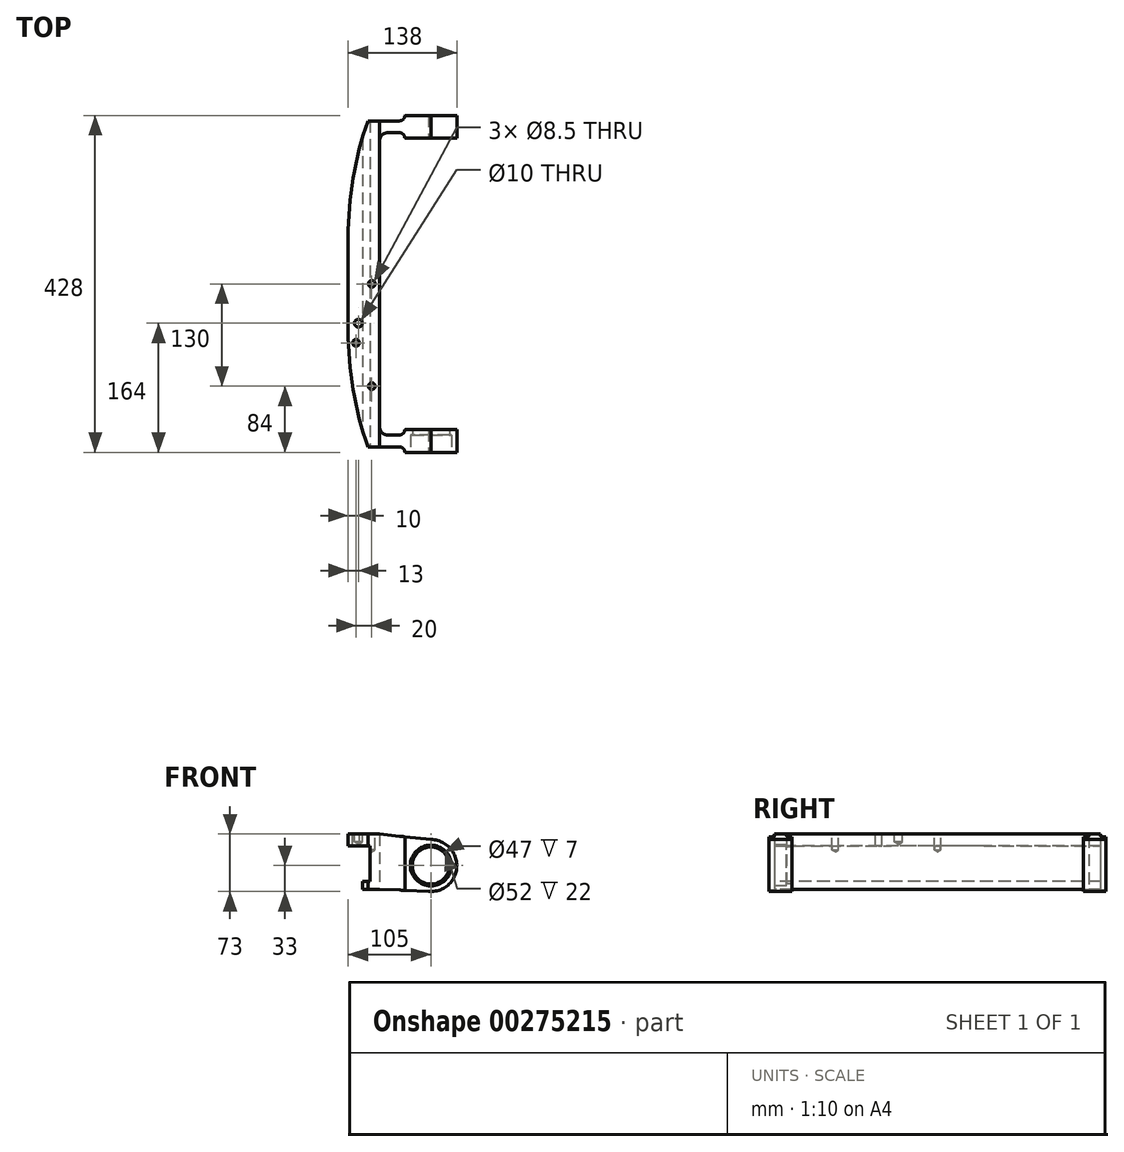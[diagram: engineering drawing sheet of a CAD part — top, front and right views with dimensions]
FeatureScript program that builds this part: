
annotation { "Feature Type Name" : "Feature", "Feature Type Description" : "" }
export const myFeature = defineFeature(function(context is Context, id is Id, definition is map)
    precondition{}
    {
        {
            var Q0;
            Q0=qCreatedBy(makeId("Top.planeOp"),FACE);
            var sketch = newSketch(context, id + "F0", { "sketchPlane" : qUnion([Q0])});
            skLineSegment(sketch, "E0", {"start": v(-134.94, 0) * mm, "end": v(159.57, 0) * mm, "construction": true});
            skLineSegment(sketch, "E1", {"start": v(0, 0) * mm, "end": v(0, 182) * mm});
            skLineSegment(sketch, "E2", {"start": v(-40, 0) * mm, "end": v(-40, 59) * mm});
            skLineSegment(sketch, "E3", {"start": v(10, 192) * mm, "end": v(25, 192) * mm});
            skLineSegment(sketch, "E4", {"start": v(32, 185) * mm, "end": v(32, 185) * mm});
            skLineSegment(sketch, "E5", {"start": v(32, 185) * mm, "end": v(98, 185) * mm});
            skLineSegment(sketch, "E6", {"start": v(98, 185) * mm, "end": v(98, 214) * mm});
            skLineSegment(sketch, "E7", {"start": v(98, 214) * mm, "end": v(32, 214) * mm});
            skLineSegment(sketch, "E8", {"start": v(32, 214) * mm, "end": v(32, 214) * mm});
            skLineSegment(sketch, "E9", {"start": v(25, 207) * mm, "end": v(-14.97, 207) * mm});
            skLineSegment(sketch, "E10", {"start": v(5.7, 199.5) * mm, "end": v(104.97, 199.5) * mm, "construction": true});
            skLineSegment(sketch, "E11.MirrorCS", {"start": v(-40, 0) * mm, "end": v(-40, -59) * mm});
            skLineSegment(sketch, "E12.MirrorCS", {"start": v(0, 0) * mm, "end": v(0, -182) * mm});
            skLineSegment(sketch, "E13.MirrorCS", {"start": v(10, -192) * mm, "end": v(32, -192) * mm});
            skLineSegment(sketch, "E14.MirrorCS", {"start": v(32, -207) * mm, "end": v(-14.97, -207) * mm});
            skLineSegment(sketch, "E15.MirrorCS", {"start": v(98, -214) * mm, "end": v(32, -214) * mm});
            skLineSegment(sketch, "E16.MirrorCS", {"start": v(32, -185) * mm, "end": v(98, -185) * mm});
            skLineSegment(sketch, "E17.MirrorCS", {"start": v(98, -185) * mm, "end": v(98, -214) * mm});
            skArc(sketch, "E18", {"start": v(-40, 59) * mm, "mid": v(-33.7, 134.05) * mm, "end": v(-14.97, 207) * mm});
            skArc(sketch, "E19.MirrorCS", {"start": v(-40, -59) * mm, "mid": v(-33.7, -134.05) * mm, "end": v(-14.97, -207) * mm});
            skLineSegment(sketch, "E20", {"start": v(65, 241.04) * mm, "end": v(65, 132.68) * mm, "construction": true});
            skPoint(sketch, "E20.endSnap0", {"position": v(65, 214) * mm});
            skPoint(sketch, "E21.visualSharp", {"position": v(0, 192) * mm});
            skArc(sketch, "E21.filletArc", {"start": v(10, 192) * mm, "mid": v(2.93, 189.07) * mm, "end": v(0, 182) * mm});
            skPoint(sketch, "E22.visualSharp", {"position": v(32, 207) * mm});
            skArc(sketch, "E22.filletArc", {"start": v(25, 207) * mm, "mid": v(29.95, 209.05) * mm, "end": v(32, 214) * mm});
            skPoint(sketch, "E23.visualSharp", {"position": v(32, 192) * mm});
            skArc(sketch, "E23.filletArc", {"start": v(32, 185) * mm, "mid": v(29.95, 189.95) * mm, "end": v(25, 192) * mm});
            skArc(sketch, "E24.MirrorCS", {"start": v(25, -207) * mm, "mid": v(29.95, -209.05) * mm, "end": v(32, -214) * mm});
            skArc(sketch, "E25.MirrorCS", {"start": v(32, -185) * mm, "mid": v(29.95, -189.95) * mm, "end": v(25, -192) * mm});
            skArc(sketch, "E26.MirrorCS", {"start": v(10, -192) * mm, "mid": v(2.93, -189.07) * mm, "end": v(0, -182) * mm});
            skPoint(sketch, "E27.orphan", {"position": v(0, -192) * mm});
            skPoint(sketch, "E28.MirrorCS.end.orphan", {"position": v(32, -185) * mm});
            skPoint(sketch, "E28.MirrorCS.start.orphan", {"position": v(32, -192) * mm});
            skPoint(sketch, "E29.MirrorCS.end.orphan", {"position": v(32, -207) * mm});
            skPoint(sketch, "E29.MirrorCS.start.orphan", {"position": v(32, -214) * mm});
            skSolve(sketch);
        }
        {
            var Q0;
            Q0=makeQuery(id+"F0.imprint","IMPRINT",FACE,{"disambiguationData":[TD([[makeQuery(id+"F0.imprint","IMPRINT",EDGE,{"derivedFrom":sQuery(id+"F0.wireOp",EDGE,"E1")}),1.0]])]});
            extrude(context, id + "F1", {"entities" : qUnion([Q0]), "endBound" : BoundingType.SYMMETRIC, "depth" : 80 * mm});
        }
        {
            var Q0;
            Q0=qCreatedBy(makeId("Front.planeOp"),FACE);
            var sketch = newSketch(context, id + "F2", { "sketchPlane" : qUnion([Q0])});
            skLineSegment(sketch, "E30.0", {"start": v(-40, 40) * mm, "end": v(-14.97, 40) * mm});
            skLineSegment(sketch, "E31.0", {"start": v(-14.97, 40) * mm, "end": v(-14.97, 40) * mm});
            skLineSegment(sketch, "E32.0", {"start": v(-14.97, -40) * mm, "end": v(-14.97, -40) * mm});
            skLineSegment(sketch, "E33.0", {"start": v(-40, -40) * mm, "end": v(-14.97, -40) * mm, "construction": true});
            skLineSegment(sketch, "E34.0", {"start": v(-40, 40) * mm, "end": v(-40, -40) * mm});
            skLineSegment(sketch, "E35", {"start": v(0, 40) * mm, "end": v(-40, 40) * mm, "construction": true});
            skLineSegment(sketch, "E36", {"start": v(0, -40) * mm, "end": v(0, 40) * mm, "construction": true});
            skLineSegment(sketch, "E37", {"start": v(-14.97, -40) * mm, "end": v(0, -40) * mm, "construction": true});
            skLineSegment(sketch, "E38", {"start": v(-40, 25) * mm, "end": v(-12, 25) * mm});
            skLineSegment(sketch, "E39", {"start": v(-12, 25) * mm, "end": v(-12, -30) * mm});
            skLineSegment(sketch, "E40", {"start": v(-12, -30) * mm, "end": v(-22, -30) * mm, "construction": true});
            skLineSegment(sketch, "E41", {"start": v(-22, -30) * mm, "end": v(-22, -40) * mm, "construction": true});
            skLineSegment(sketch, "E42", {"start": v(-12, -20) * mm, "end": v(-22, -20) * mm});
            skLineSegment(sketch, "E43", {"start": v(-22, -20) * mm, "end": v(-22, -30) * mm});
            skLineSegment(sketch, "E44", {"start": v(-12, -30) * mm, "end": v(0, -30) * mm});
            skLineSegment(sketch, "E45", {"start": v(-22, -30) * mm, "end": v(-40, -30) * mm});
            skSolve(sketch);
        }
        {
            var Q0;
            Q0 = qSketchRegion(id + "F2", true);
            extrude(context, id + "F3", {"entities" : qUnion([Q0]), "operationType" : NewBodyOperationType.REMOVE, "endBound" : BoundingType.SYMMETRIC, "oppositeDirection" : true, "depth" : 464 * mm});
        }
        {
            var Q0;
            Q0=makeQuery(id+"F1.opExtrude","SWEPT_FACE",FACE,{"disambiguationData":[OSD([sQuery(id+"F0.wireOp",EDGE,"E15.MirrorCS")])]});
            var sketch = newSketch(context, id + "F4", { "sketchPlane" : qUnion([Q0])});
            skArc(sketch, "E46", {"start": v(51.25, -30) * mm, "mid": v(97.24, -7.04) * mm, "end": v(65, 33) * mm});
            skLineSegment(sketch, "E47.0", {"start": v(25, 40) * mm, "end": v(-14.97, 40) * mm});
            skLineSegment(sketch, "E48", {"start": v(65, 33) * mm, "end": v(0, 40) * mm});
            skPoint(sketch, "E48.endSnap0", {"position": v(5.02, 40) * mm});
            skPoint(sketch, "E49.0", {"position": v(-22, -30) * mm});
            skLineSegment(sketch, "E50", {"start": v(-22, -30) * mm, "end": v(145.28, -30) * mm, "construction": true});
            skLineSegment(sketch, "E51", {"start": v(0, -30) * mm, "end": v(65, -33) * mm});
            skLineSegment(sketch, "E52", {"start": v(0, -30) * mm, "end": v(-22, -30) * mm});
            skLineSegment(sketch, "E53", {"start": v(-22, -30) * mm, "end": v(-78.33, -18.72) * mm});
            skLineSegment(sketch, "E54", {"start": v(-78.33, -18.72) * mm, "end": v(-54.2, -117.22) * mm});
            skLineSegment(sketch, "E55", {"start": v(-54.2, -117.22) * mm, "end": v(170.9, -100.97) * mm});
            skLineSegment(sketch, "E56", {"start": v(170.9, -100.97) * mm, "end": v(118.58, -39.9) * mm});
            skLineSegment(sketch, "E57", {"start": v(118.58, -39.9) * mm, "end": v(129.42, 78.8) * mm});
            skLineSegment(sketch, "E58", {"start": v(129.42, 78.8) * mm, "end": v(5.79, 93.58) * mm});
            skLineSegment(sketch, "E59", {"start": v(5.79, 93.58) * mm, "end": v(5.02, 40) * mm});
            skSolve(sketch);
        }
        {
            var Q0;
            {var subQ13=sQuery(id+"F4.wireOp",EDGE,"E52");Q0=makeQuery(id+"F4.imprint","IMPRINT",FACE,{"disambiguationData":[TD([[makeQuery(id+"F4.imprint","IMPRINT",EDGE,{"derivedFrom":subQ13}),1.0]])]});}
            var Q1;
            {var subQ0=sQuery(id+"F0.wireOp",EDGE,"E15.MirrorCS");var subQ1=makeQuery(id+"F1.opExtrude","CAP_EDGE",EDGE,{"disambiguationData":[OSD([subQ0])],"isStart":false});Q1=makeQuery(id+"F4.imprint","IMPRINT",FACE,{"disambiguationData":[TD([[makeQuery(id+"F4.imprint","IMPRINT",EDGE,{"derivedFrom":subQ1}),1.0]])]});}
            var Q2;
            {var subQ0=sQuery(id+"F0.wireOp",EDGE,"E15.MirrorCS");var subQ1=makeQuery(id+"F1.opExtrude","CAP_EDGE",EDGE,{"disambiguationData":[OSD([subQ0])],"isStart":true});Q2=makeQuery(id+"F4.imprint","IMPRINT",FACE,{"disambiguationData":[TD([[makeQuery(id+"F4.imprint","IMPRINT",EDGE,{"derivedFrom":subQ1}),-1.0]])]});}
            extrude(context, id + "F5", {"entities" : qUnion([Q0, Q1, Q2]), "operationType" : NewBodyOperationType.REMOVE, "endBound" : BoundingType.THROUGH_ALL, "oppositeDirection" : true, "depth" : 25 * mm});
        }
        {
            var Q0;
            Q0=makeQuery(id+"F1.opExtrude","SWEPT_FACE",FACE,{"disambiguationData":[OSD([sQuery(id+"F0.wireOp",EDGE,"E15.MirrorCS")])]});
            var sketch = newSketch(context, id + "F6", { "sketchPlane" : qUnion([Q0])});
            skArc(sketch, "E60.0", {"start": v(61.96, -32.86) * mm, "mid": v(97.96, -1.52) * mm, "end": v(65, 33) * mm});
            skCircle(sketch, "E61", {"center": v(65, 0) * mm, "radius": 26 * mm});
            skCircle(sketch, "E62", {"center": v(65, 0) * mm, "radius": 23.5 * mm});
            skSolve(sketch);
        }
        {
            var Q0;
            Q0=makeQuery(id+"F6.imprint","IMPRINT",FACE,{"disambiguationData":[TD([[makeQuery(id+"F6.imprint","IMPRINT",EDGE,{"derivedFrom":sQuery(id+"F6.wireOp",EDGE,"E62")}),1.0]])]});
            extrude(context, id + "F7", {"entities" : qUnion([Q0]), "operationType" : NewBodyOperationType.REMOVE, "oppositeDirection" : true, "depth" : 61.2 * mm});
        }
        {
            var Q0;
            Q0=makeQuery(id+"F6.imprint","IMPRINT",FACE,{"disambiguationData":[TD([[makeQuery(id+"F6.imprint","IMPRINT",EDGE,{"derivedFrom":sQuery(id+"F6.wireOp",EDGE,"E61")}),1.0]])]});
            extrude(context, id + "F8", {"entities" : qUnion([Q0]), "operationType" : NewBodyOperationType.REMOVE, "oppositeDirection" : true, "depth" : 22 * mm});
        }
        {
            var Q0;
            Q0=makeQuery(id+"F1.opExtrude","CAP_FACE",FACE,{"disambiguationData":[OSD([sQuery(id+"F0.wireOp",EDGE,"E1"),sQuery(id+"F0.wireOp",EDGE,"E2"),sQuery(id+"F0.wireOp",EDGE,"E3"),sQuery(id+"F0.wireOp",EDGE,"E5"),sQuery(id+"F0.wireOp",EDGE,"E6"),sQuery(id+"F0.wireOp",EDGE,"E7"),sQuery(id+"F0.wireOp",EDGE,"E9"),sQuery(id+"F0.wireOp",EDGE,"E11.MirrorCS"),sQuery(id+"F0.wireOp",EDGE,"E12.MirrorCS"),sQuery(id+"F0.wireOp",EDGE,"E13.MirrorCS"),sQuery(id+"F0.wireOp",EDGE,"E14.MirrorCS"),sQuery(id+"F0.wireOp",EDGE,"E15.MirrorCS"),sQuery(id+"F0.wireOp",EDGE,"E16.MirrorCS"),sQuery(id+"F0.wireOp",EDGE,"E17.MirrorCS"),sQuery(id+"F0.wireOp",EDGE,"E18"),sQuery(id+"F0.wireOp",EDGE,"E19.MirrorCS"),sQuery(id+"F0.wireOp",EDGE,"E21.filletArc"),sQuery(id+"F0.wireOp",EDGE,"E22.filletArc"),sQuery(id+"F0.wireOp",EDGE,"E23.filletArc"),sQuery(id+"F0.wireOp",EDGE,"E24.MirrorCS"),sQuery(id+"F0.wireOp",EDGE,"E25.MirrorCS"),sQuery(id+"F0.wireOp",EDGE,"E26.MirrorCS")])],"isStart":false});
            var sketch = newSketch(context, id + "F9", { "sketchPlane" : qUnion([Q0])});
            skPoint(sketch, "E63", {"position": v(-10, -130) * mm});
            skPoint(sketch, "E64", {"position": v(-30, -75) * mm});
            skPoint(sketch, "E65", {"position": v(-27, -50) * mm});
            skPoint(sketch, "E66", {"position": v(-10, 0) * mm});
            skSolve(sketch);
        }
        {
            var Q0;
            Q0=sQuery(id+"F9.wireOp",VERTEX,"E65");
            var Q1;
            Q1=makeQuery(id+"F1.opExtrude","SWEPT_BODY",BODY,{"disambiguationData":[OSD([sQuery(id+"F0.wireOp",EDGE,"E1"),sQuery(id+"F0.wireOp",EDGE,"E2"),sQuery(id+"F0.wireOp",EDGE,"E3"),sQuery(id+"F0.wireOp",EDGE,"E5"),sQuery(id+"F0.wireOp",EDGE,"E6"),sQuery(id+"F0.wireOp",EDGE,"E7"),sQuery(id+"F0.wireOp",EDGE,"E9"),sQuery(id+"F0.wireOp",EDGE,"E11.MirrorCS"),sQuery(id+"F0.wireOp",EDGE,"E12.MirrorCS"),sQuery(id+"F0.wireOp",EDGE,"E13.MirrorCS"),sQuery(id+"F0.wireOp",EDGE,"E14.MirrorCS"),sQuery(id+"F0.wireOp",EDGE,"E15.MirrorCS"),sQuery(id+"F0.wireOp",EDGE,"E16.MirrorCS"),sQuery(id+"F0.wireOp",EDGE,"E17.MirrorCS"),sQuery(id+"F0.wireOp",EDGE,"E18"),sQuery(id+"F0.wireOp",EDGE,"E19.MirrorCS"),sQuery(id+"F0.wireOp",EDGE,"E21.filletArc"),sQuery(id+"F0.wireOp",EDGE,"E22.filletArc"),sQuery(id+"F0.wireOp",EDGE,"E23.filletArc"),sQuery(id+"F0.wireOp",EDGE,"E24.MirrorCS"),sQuery(id+"F0.wireOp",EDGE,"E25.MirrorCS"),sQuery(id+"F0.wireOp",EDGE,"E26.MirrorCS")])]});
            hole(context, id + "F10", {"style" : HoleStyle.SIMPLE, "endStyle" : HoleEndStyle.BLIND, "holeDiameter" : 10 * mm, "holeDepth" : 10 * mm, "tappedDepth" : 12 * mm, "tapClearance" : 3, "locations" : qUnion([Q0]), "scope" : qUnion([Q1])});
        }
        {
            var Q0;
            Q0=sQuery(id+"F9.wireOp",VERTEX,"E64");
            var Q1;
            Q1=sQuery(id+"F9.wireOp",VERTEX,"E63");
            var Q2;
            Q2=sQuery(id+"F9.wireOp",VERTEX,"E66");
            var Q3;
            Q3=makeQuery(id+"F1.opExtrude","SWEPT_BODY",BODY,{"disambiguationData":[OSD([sQuery(id+"F0.wireOp",EDGE,"E1"),sQuery(id+"F0.wireOp",EDGE,"E2"),sQuery(id+"F0.wireOp",EDGE,"E3"),sQuery(id+"F0.wireOp",EDGE,"E5"),sQuery(id+"F0.wireOp",EDGE,"E6"),sQuery(id+"F0.wireOp",EDGE,"E7"),sQuery(id+"F0.wireOp",EDGE,"E9"),sQuery(id+"F0.wireOp",EDGE,"E11.MirrorCS"),sQuery(id+"F0.wireOp",EDGE,"E12.MirrorCS"),sQuery(id+"F0.wireOp",EDGE,"E13.MirrorCS"),sQuery(id+"F0.wireOp",EDGE,"E14.MirrorCS"),sQuery(id+"F0.wireOp",EDGE,"E15.MirrorCS"),sQuery(id+"F0.wireOp",EDGE,"E16.MirrorCS"),sQuery(id+"F0.wireOp",EDGE,"E17.MirrorCS"),sQuery(id+"F0.wireOp",EDGE,"E18"),sQuery(id+"F0.wireOp",EDGE,"E19.MirrorCS"),sQuery(id+"F0.wireOp",EDGE,"E21.filletArc"),sQuery(id+"F0.wireOp",EDGE,"E22.filletArc"),sQuery(id+"F0.wireOp",EDGE,"E23.filletArc"),sQuery(id+"F0.wireOp",EDGE,"E24.MirrorCS"),sQuery(id+"F0.wireOp",EDGE,"E25.MirrorCS"),sQuery(id+"F0.wireOp",EDGE,"E26.MirrorCS")])]});
            hole(context, id + "F11", {"style" : HoleStyle.SIMPLE, "endStyle" : HoleEndStyle.BLIND, "standardTappedOrClearance" : lookupTablePath({ "standard" : "ISO", "engagement" : "75%", "pitch" : "1.5 mm", "size" : "M10", "type" : "Tapped" }), "standardBlindInLast" : lookupTablePath({ "standard" : "ISO", "engagement" : "75%", "pitch" : "1.5 mm", "size" : "M10", "type" : "Tapped" }), "holeDiameter" : 8.5 * mm, "showTappedDepth" : true, "holeDepth" : 20 * mm, "tappedDepth" : 15.5 * mm, "tapClearance" : 3, "locations" : qUnion([Q0, Q1, Q2]), "scope" : qUnion([Q3]), "majorDiameter" : 10 * mm});
        }
    });
